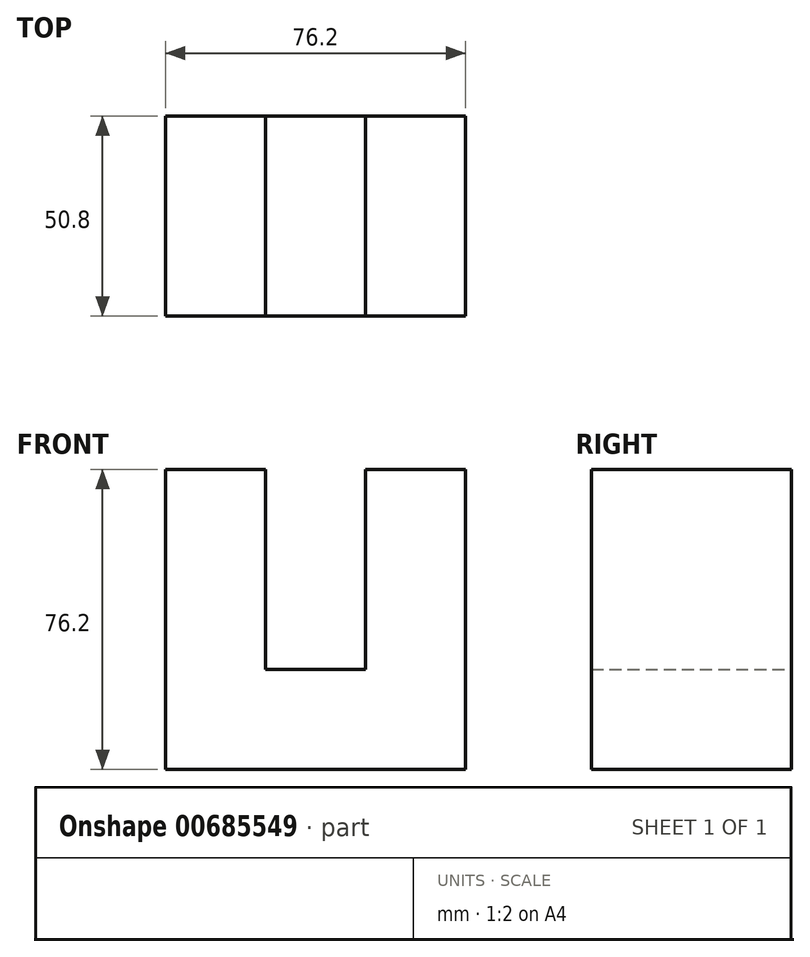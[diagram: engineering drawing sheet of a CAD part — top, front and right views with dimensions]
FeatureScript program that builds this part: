
annotation { "Feature Type Name" : "Feature", "Feature Type Description" : "" }
export const myFeature = defineFeature(function(context is Context, id is Id, definition is map)
    precondition{}
    {
        {
            var Q0;
            Q0=qCreatedBy(makeId("Front.planeOp"),FACE);
            var sketch = newSketch(context, id + "F0", { "sketchPlane" : qUnion([Q0])});
            skLineSegment(sketch, "E0", {"start": v(0, 0) * mm, "end": v(0, 76.2) * mm});
            skLineSegment(sketch, "E1", {"start": v(0, 76.2) * mm, "end": v(-25.4, 76.2) * mm});
            skLineSegment(sketch, "E2", {"start": v(-25.4, 76.2) * mm, "end": v(-25.4, 25.4) * mm});
            skLineSegment(sketch, "E3", {"start": v(-25.4, 25.4) * mm, "end": v(-50.8, 25.4) * mm});
            skLineSegment(sketch, "E4", {"start": v(-50.8, 25.4) * mm, "end": v(-50.8, 76.2) * mm});
            skLineSegment(sketch, "E5", {"start": v(-50.8, 76.2) * mm, "end": v(-76.2, 76.2) * mm});
            skLineSegment(sketch, "E6", {"start": v(-76.2, 76.2) * mm, "end": v(-76.2, 0) * mm});
            skLineSegment(sketch, "E7", {"start": v(-76.2, 0) * mm, "end": v(0, 0) * mm});
            skSolve(sketch);
        }
        {
            var Q0;
            Q0 = qSketchRegion(id + "F0", true);
            extrude(context, id + "F1", {"entities" : qUnion([Q0]), "depth" : 50.8 * mm, "offsetDistance" : 25.4 * mm});
        }
    });
